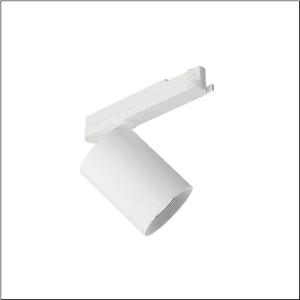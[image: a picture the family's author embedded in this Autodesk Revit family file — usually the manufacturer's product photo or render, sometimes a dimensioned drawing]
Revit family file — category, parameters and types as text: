
# Revit family: spot_11_51sd14mba5a
name_source: partatom
category: Lighting Fixtures
units: mm (PartAtom-declared; Revit-internal decimal feet)

## family parameters
Cut with Voids When Loaded = No
Host = Face
Light Source = No
Part Type = Normal
Room Calculation Point = No
Round Connector Dimension = Use Diameter
Shared = No

## types (1)
- --- (1 x LED, 7210 lm, 50.7 W, 2700K)
    Apparent Load = 51 VA
    CIE Flux Codes = 95 98 100 100 100
    Color Rendering = 90
    Color Temperature = 2700K
    Default Elevation = 1800 mm
    Description = Spot 11, directional spotlight, light control with lens, of PMMA, LED rated luminous flux: 5.550lm, light colour: 927, control gear: ECG Multilumen, with 3-phase adapter, mains connection: 220..240V, AC, 50/60Hz, of aluminium, traffic white (RAL 9016), length: 213mm, diameter: 105mm, protection rating (complete): IP20, insulation class (complete): insulation class I (protective earthing), certification: CE, impact resistance: IK02, permissible ambient temperature for indoor applications: -20..+40°C, packaging unit: 1 piece
    Height = 175 mm
    Lamp = 1 x LED
    Lamp Light Flux = 7210 lm
    Lamp Power = 50.7 W
    Lamp count = 1
    Length = 105 mm
    Luminous efficacy = 142 lm/W
    Manufacturer = Siteco
    ModVariant = No
    Model = 51SD14MBA5A
    Mounting Place = Ceiling
    Mounting Type = Pendant
    Number of Poles = 1
    OnlyDefault = Yes
    Power Factor = 1
    Product Name = Spot 11
    Product group = directional spotlight
    ProductGroupID = 905
    Protection Class = Protection class I
    Protection Degree = IP 20
    RLX_Detail_Level = 1
    RLX_Emergency_Light_Flux = 0 lm
    RLX_Emergency_Type = 0
    RLX_Emergency_Type_DB = No
    RlxData = <blob elided: 17669 chars, md5=302b0e74>
    Socket = socket
    Standby Power = 0 W
    System Light Flux = 7210 lm
    System Power = 51 W
    Type Comments = factory setting: luminous flux: 100 % | (ON | ON | ON | ON) | 1050 mA
    Type Image = l_1006697.jpg
    URL = http://relux.com
    VarID = @adj_148557
    Voltage = 0 V
    Weight = 0.00 kg
    Width = 0 mm  [stored 0 ft]

note: [stored X ft] marks values corroborated as IEEE doubles in the binary element streams (Revit-internal decimal feet)

## geometry (parser evidence)
native form markers: Blend x4, Sweep x10
no freeform markers — native parametric forms only
